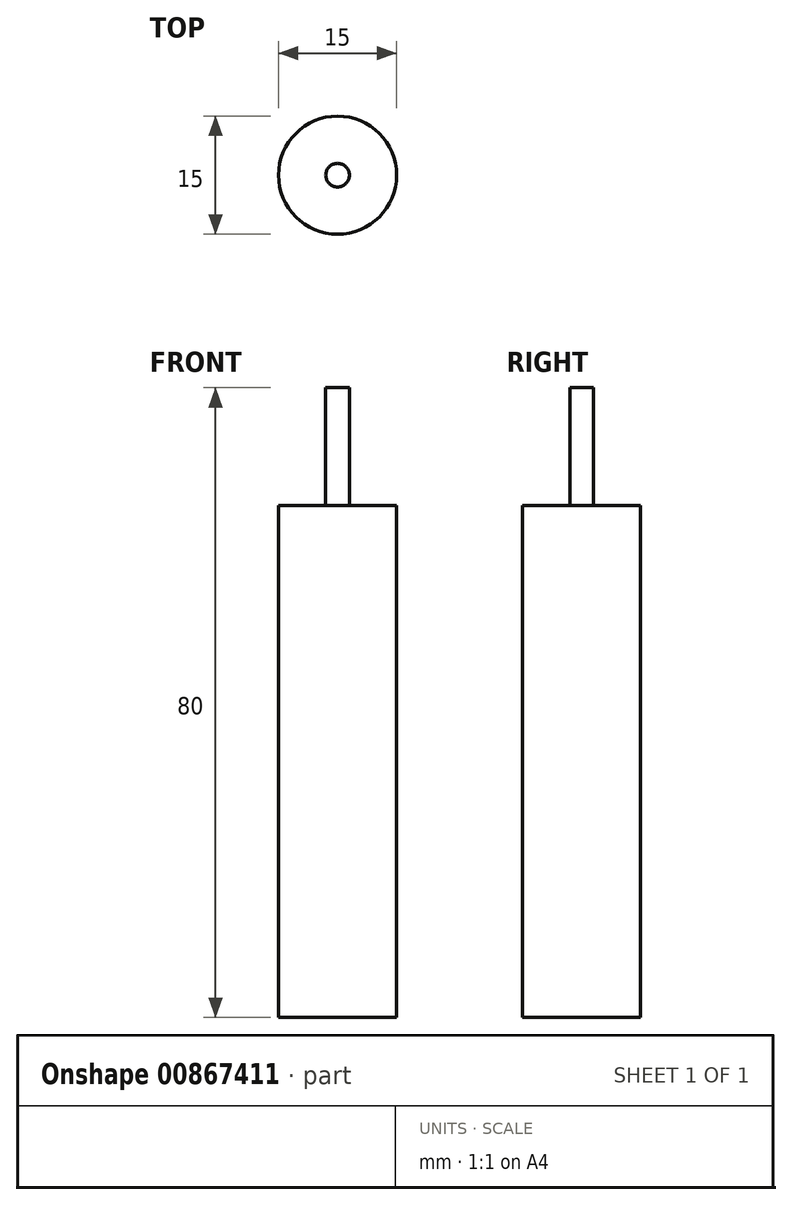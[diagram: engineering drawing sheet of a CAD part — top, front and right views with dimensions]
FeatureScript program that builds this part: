
annotation { "Feature Type Name" : "Feature", "Feature Type Description" : "" }
export const myFeature = defineFeature(function(context is Context, id is Id, definition is map)
    precondition{}
    {
        {
            var Q0;
            Q0=qCreatedBy(makeId("Top.planeOp"),FACE);
            var sketch = newSketch(context, id + "F0", { "sketchPlane" : qUnion([Q0])});
            skCircle(sketch, "E0", {"center": v(0, 0) * mm, "radius": 7.5 * mm});
            skSolve(sketch);
        }
        {
            var Q0;
            Q0=qSketchRegion(id+"F0",true);
            extrude(context, id + "F1", {"entities" : qUnion([Q0]), "endBound" : BoundingType.SYMMETRIC, "depth" : 65 * mm, "offsetDistance" : 25 * mm});
        }
        {
            var Q0;
            Q0=makeQuery(id+"F1.opExtrude","CAP_FACE",FACE,{"disambiguationData":[OSD([sQuery(id+"F0.wireOp",EDGE,"E0")])],"isStart":false});
            var sketch = newSketch(context, id + "F2", { "sketchPlane" : qUnion([Q0])});
            skCircle(sketch, "E1", {"center": v(0, 0) * mm, "radius": 1.5 * mm});
            skSolve(sketch);
        }
        {
            var Q0;
            Q0=qSketchRegion(id+"F2",true);
            extrude(context, id + "F3", {"entities" : qUnion([Q0]), "operationType" : NewBodyOperationType.ADD, "depth" : 15 * mm, "offsetDistance" : 25 * mm});
        }
    });
